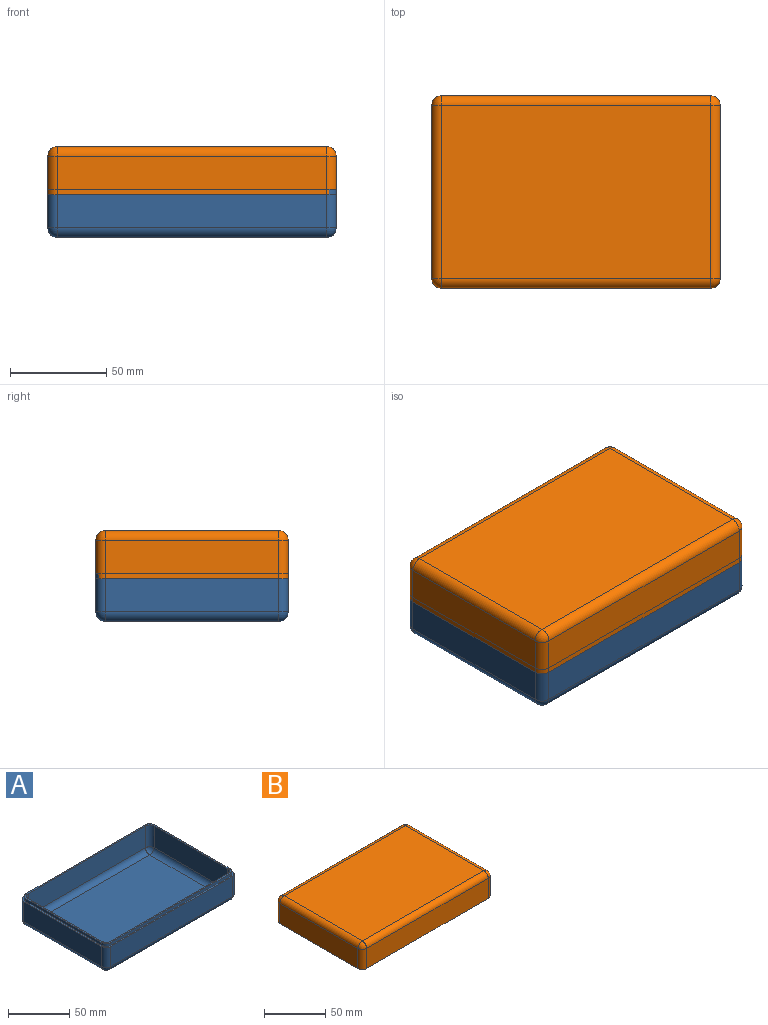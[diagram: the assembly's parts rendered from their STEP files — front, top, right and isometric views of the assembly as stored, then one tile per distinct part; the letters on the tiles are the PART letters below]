
ASSEMBLY  parts=2 mates=1
PART A: 44 faces, bbox 150x100x27.9 mm
  f0: plane 150x100mm, normal (0,0,1), area 618.8mm2, adj f1,f2,f3,f4,f6,f8,f11,f17
  f1: plane 140x20mm, normal (0,-1,0), area 2800mm2, adj f0,f8,f14,f17
  f2: plane 90x20mm, normal (1,0,0), area 1800mm2, adj f0,f11,f15,f17
  f3: plane 140x20mm, normal (0,1,0), area 2800mm2, adj f0,f6,f10,f11
  f4: plane 90x20mm, normal (-1,0,0), area 1800mm2, adj f0,f6,f8,f9
  f5: plane 140x90mm, normal (0,0,-1), area 12600mm2, adj f9,f10,f14,f15
  f6: cylinder r=5mm len=20mm, axis (0,0,1), area 157.1mm2, adj f0,f3,f4,f7
  f7: sphere r=5mm, area 39.3mm2, adj f6,f9,f10
  f8: cylinder r=5mm len=20mm, axis (0,0,-1), area 157.1mm2, adj f0,f1,f4,f12
  f9: cylinder r=5mm len=90mm, axis (0,-1,0), area 706.9mm2, adj f4,f5,f7,f12
  f10: cylinder r=5mm len=140mm, axis (-1,0,0), area 1099.6mm2, adj f3,f5,f7,f13
  f11: cylinder r=5mm len=20mm, axis (0,0,-1), area 157.1mm2, adj f0,f2,f3,f13
  f12: sphere r=5mm, area 39.3mm2, adj f8,f9,f14
  f13: sphere r=5mm, area 39.3mm2, adj f10,f11,f15
  f14: cylinder r=5mm len=140mm, axis (1,0,0), area 1099.6mm2, adj f1,f5,f12,f16
  f15: cylinder r=5mm len=90mm, axis (0,1,0), area 706.9mm2, adj f2,f5,f13,f16
  f16: sphere r=5mm, area 39.3mm2, adj f14,f15,f17
  f17: cylinder r=5mm len=20mm, axis (0,0,1), area 157.1mm2, adj f0,f1,f2,f16
  f18: plane 137.5x2.75mm, normal (0,-1,0), area 378.1mm2, adj f0,f19,f25,f26
  f19: cylinder r=5mm len=5mm, axis (0,0,-1), area 21.6mm2, adj f0,f18,f20,f26
  f20: plane 87.5x2.75mm, normal (1,0,0), area 240.6mm2, adj f0,f19,f21,f26
  f21: cylinder r=5mm len=5mm, axis (0,0,-1), area 21.6mm2, adj f0,f20,f22,f26
  f22: plane 137.5x2.75mm, normal (0,1,0), area 378.1mm2, adj f0,f21,f23,f26
  f23: cylinder r=5mm len=5mm, axis (0,0,-1), area 21.6mm2, adj f0,f22,f24,f26
  f24: plane 87.5x2.75mm, normal (-1,0,0), area 240.6mm2, adj f0,f23,f25,f26
  f25: cylinder r=5mm len=5mm, axis (0,0,-1), area 21.6mm2, adj f0,f18,f24,f26
  f26: plane 147.5x97.5mm, normal (0,0,1), area 606.2mm2, adj f18,f19,f20,f21,f22,f23,f24,f25
  f27: plane 132.86x82.86mm, normal (0,0,1), area 11009.6mm2, adj f28,f30,f32,f34
  f28: cylinder r=5mm len=132.86mm, axis (1,0,0), area 1008.7mm2, adj f27,f29,f35,f43
  f29: sphere r=5mm, area 36.7mm2, adj f28,f30,f42
  f30: cylinder r=5mm len=82.86mm, axis (0,-1,0), area 629.1mm2, adj f27,f29,f31,f41
  f31: sphere r=5mm, area 36.7mm2, adj f30,f32,f40
  f32: cylinder r=5mm len=132.86mm, axis (1,0,0), area 1008.7mm2, adj f27,f31,f33,f39
  f33: sphere r=5mm, area 36.7mm2, adj f32,f34,f38
  f34: cylinder r=5mm len=82.86mm, axis (0,-1,0), area 629.1mm2, adj f27,f33,f35,f37
  f35: sphere r=5mm, area 36.7mm2, adj f28,f34,f36
  f36: cylinder r=5mm len=20.73mm, axis (0.05,-0.05,1), area 161.8mm2, adj f26,f35,f37,f43
  f37: plane 85.01x20.51mm, normal (-1,0,0.05), area 1724.1mm2, adj f26,f34,f36,f38
  f38: cylinder r=5mm len=20.73mm, axis (0.05,0.05,1), area 161.8mm2, adj f26,f33,f37,f39
  f39: plane 135.01x20.51mm, normal (0,-1,0.05), area 2751.1mm2, adj f26,f32,f38,f40
  f40: cylinder r=5mm len=20.73mm, axis (-0.05,0.05,1), area 161.8mm2, adj f26,f31,f39,f41
  f41: plane 85.01x20.51mm, normal (1,0,0.05), area 1724.1mm2, adj f26,f30,f40,f42
  f42: cylinder r=5mm len=20.73mm, axis (-0.05,-0.05,1), area 161.8mm2, adj f26,f29,f41,f43
  f43: plane 135.01x20.51mm, normal (0,1,0.05), area 2751.1mm2, adj f26,f28,f36,f42
PART B: 44 faces, bbox 150x100x25 mm
  f0: plane 150x100mm, normal (0,0,-1), area 618.7mm2, adj f1,f2,f3,f4,f6,f8,f11,f17
  f1: plane 140x20mm, normal (0,-1,0), area 2800mm2, adj f0,f8,f14,f17
  f2: plane 90x20mm, normal (1,0,0), area 1800mm2, adj f0,f11,f15,f17
  f3: plane 140x20mm, normal (0,1,0), area 2800mm2, adj f0,f6,f10,f11
  f4: plane 90x20mm, normal (-1,0,0), area 1800mm2, adj f0,f6,f8,f9
  f5: plane 140x90mm, normal (0,0,1), area 12600mm2, adj f9,f10,f14,f15
  f6: cylinder r=5mm len=20mm, axis (0,0,-1), area 157.1mm2, adj f0,f3,f4,f7
  f7: sphere r=5mm, area 39.3mm2, adj f6,f9,f10
  f8: cylinder r=5mm len=20mm, axis (0,0,1), area 157.1mm2, adj f0,f1,f4,f12
  f9: cylinder r=5mm len=90mm, axis (0,-1,0), area 706.9mm2, adj f4,f5,f7,f12
  f10: cylinder r=5mm len=140mm, axis (-1,0,0), area 1099.6mm2, adj f3,f5,f7,f13
  f11: cylinder r=5mm len=20mm, axis (0,0,1), area 157.1mm2, adj f0,f2,f3,f13
  f12: sphere r=5mm, area 39.3mm2, adj f8,f9,f14
  f13: sphere r=5mm, area 39.3mm2, adj f10,f11,f15
  f14: cylinder r=5mm len=140mm, axis (1,0,0), area 1099.6mm2, adj f1,f5,f12,f16
  f15: cylinder r=5mm len=90mm, axis (0,1,0), area 706.9mm2, adj f2,f5,f13,f16
  f16: sphere r=5mm, area 39.3mm2, adj f14,f15,f17
  f17: cylinder r=5mm len=20mm, axis (0,0,-1), area 157.1mm2, adj f0,f1,f2,f16
  f18: plane 87.5x2.75mm, normal (-1,0,0), area 240.6mm2, adj f0,f19,f25,f26
  f19: cylinder r=5mm len=5mm, axis (0,0,-1), area 21.6mm2, adj f0,f18,f20,f26
  f20: plane 137.5x2.75mm, normal (0,1,0), area 378.1mm2, adj f0,f19,f21,f26
  f21: cylinder r=5mm len=5mm, axis (0,0,-1), area 21.6mm2, adj f0,f20,f22,f26
  f22: plane 87.5x2.75mm, normal (1,0,0), area 240.6mm2, adj f0,f21,f23,f26
  f23: cylinder r=5mm len=5mm, axis (0,0,-1), area 21.6mm2, adj f0,f22,f24,f26
  f24: plane 137.5x2.75mm, normal (0,-1,0), area 378.1mm2, adj f0,f23,f25,f26
  f25: cylinder r=5mm len=5mm, axis (0,0,-1), area 21.6mm2, adj f0,f18,f24,f26
  f26: plane 147.5x97.5mm, normal (0,0,-1), area 606.2mm2, adj f18,f19,f20,f21,f22,f23,f24,f25
  f27: plane 133.44x83.44mm, normal (0,0,-1), area 11134.3mm2, adj f28,f29,f30,f31
  f28: cylinder r=5mm len=133.44mm, axis (1,0,0), area 1013.1mm2, adj f27,f32,f33,f43
  f29: cylinder r=5mm len=83.44mm, axis (0,-1,0), area 633.5mm2, adj f27,f32,f34,f42
  f30: cylinder r=5mm len=133.44mm, axis (1,0,0), area 1013.1mm2, adj f27,f34,f35,f40
  f31: cylinder r=5mm len=83.44mm, axis (0,-1,0), area 633.5mm2, adj f27,f33,f35,f38
  f32: sphere r=5mm, area 36.7mm2, adj f28,f29,f41
  f33: sphere r=5mm, area 36.7mm2, adj f28,f31,f37
  f34: sphere r=5mm, area 36.7mm2, adj f29,f30,f39
  f35: sphere r=5mm, area 36.7mm2, adj f30,f31,f36
  f36: cylinder r=5mm len=15.23mm, axis (0.05,-0.05,1), area 118.6mm2, adj f26,f35,f38,f40
  f37: cylinder r=5mm len=15.23mm, axis (0.05,0.05,1), area 118.6mm2, adj f26,f33,f38,f43
  f38: plane 85.01x15.01mm, normal (1,0,-0.05), area 1266.1mm2, adj f26,f31,f36,f37
  f39: cylinder r=5mm len=15.23mm, axis (-0.05,-0.05,1), area 118.6mm2, adj f26,f34,f40,f42
  f40: plane 135.01x15.01mm, normal (0,-1,-0.05), area 2017.7mm2, adj f26,f30,f36,f39
  f41: cylinder r=5mm len=15.23mm, axis (-0.05,0.05,1), area 118.6mm2, adj f26,f32,f42,f43
  f42: plane 85.01x15.01mm, normal (-1,0,-0.05), area 1266.1mm2, adj f26,f29,f39,f41
  f43: plane 135.01x15.01mm, normal (0,1,-0.05), area 2017.7mm2, adj f26,f28,f37,f41
PLACE A t=(29.39,-7.15,14.94)mm
PLACE B t=(29.39,-7.15,-45.81)mm
MATE slider A.f26 <-> B.f26  axis (0,0,1) through (29.39,-7.15,-11.31)mm
